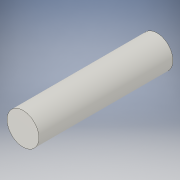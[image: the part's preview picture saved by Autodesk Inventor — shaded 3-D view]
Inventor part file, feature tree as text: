
AUTODESK INVENTOR PART (.ipt)
format: ipt  version: 2018 (Build 220112000, 112)  size: 86,528 bytes
history: native  units: in
note: dims shown in document units (in); Inventor stores cm internally (conversion verified against a paired STEP export)
features: extrude x1, sketch x1
ambient origin geometry x8: Origin, YZ Plane, XZ Plane, XY Plane, X Axis, Y Axis, Z Axis, Center Point
bodies: Solid1 (feature_tree)
feature tree (2):
  extrude  "Extrusion1"  Depth=3.2795in TaperAngle=0.0deg
  sketch  "Sketch1"  dims[d0=0.7795in d1=3.2795in d2=0.0in]
